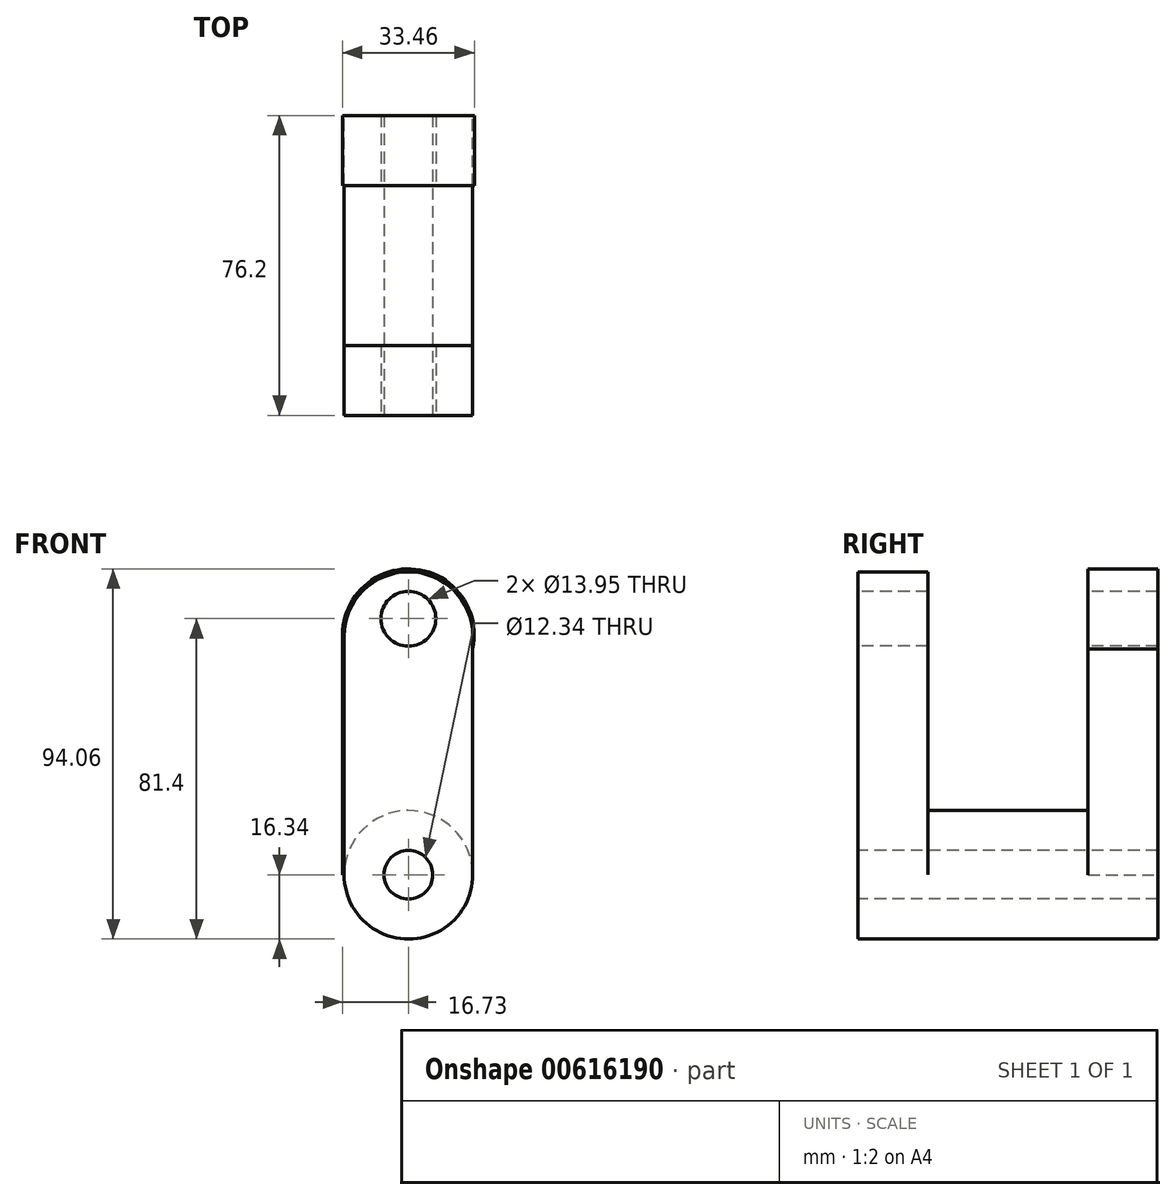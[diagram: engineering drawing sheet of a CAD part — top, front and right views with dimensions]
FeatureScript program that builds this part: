
annotation { "Feature Type Name" : "Feature", "Feature Type Description" : "" }
export const myFeature = defineFeature(function(context is Context, id is Id, definition is map)
    precondition{}
    {
        {
            var Q0;
            Q0=qCreatedBy(makeId("Front.planeOp"),FACE);
            var sketch = newSketch(context, id + "F0", { "sketchPlane" : qUnion([Q0])});
            skCircle(sketch, "E0", {"center": v(0, 0) * mm, "radius": 16.34 * mm});
            skSolve(sketch);
        }
        {
            var Q0;
            Q0 = qSketchRegion(id + "F0", true);
            extrude(context, id + "F1", {"entities" : qUnion([Q0]), "depth" : 38.1 * mm, "offsetDistance" : 25.4 * mm});
        }
        {
            var Q0;
            Q0 = qSketchRegion(id + "F0", true);
            extrude(context, id + "F2", {"entities" : qUnion([Q0]), "operationType" : NewBodyOperationType.ADD, "depth" : -38.1 * mm, "offsetDistance" : 25.4 * mm});
        }
        {
            var Q0;
            Q0=makeQuery(id+"F1.opExtrude","CAP_FACE",FACE,{"disambiguationData":[OSD([sQuery(id+"F0.wireOp",EDGE,"E0")])],"isStart":false});
            var sketch = newSketch(context, id + "F3", { "sketchPlane" : qUnion([Q0])});
            skLineSegment(sketch, "E1.bottom", {"start": v(-16.34, 0) * mm, "end": v(16.34, 0) * mm});
            skLineSegment(sketch, "E1.top", {"start": v(-16.34, 60.62) * mm, "end": v(16.34, 60.62) * mm});
            skLineSegment(sketch, "E1.left", {"start": v(-16.34, 0) * mm, "end": v(-16.34, 60.62) * mm});
            skLineSegment(sketch, "E1.right", {"start": v(16.34, 0) * mm, "end": v(16.34, 60.62) * mm});
            skCircle(sketch, "E2", {"center": v(0, 60.62) * mm, "radius": 16.34 * mm});
            skSolve(sketch);
        }
        {
            var Q0;
            Q0=makeQuery(id+"F2.opExtrude","CAP_FACE",FACE,{"disambiguationData":[OSD([sQuery(id+"F0.wireOp",EDGE,"E0")])],"isStart":false});
            var sketch = newSketch(context, id + "F4", { "sketchPlane" : qUnion([Q0])});
            skLineSegment(sketch, "E3.bottom", {"start": v(-16.34, 0) * mm, "end": v(16.73, 0) * mm});
            skLineSegment(sketch, "E3.top", {"start": v(-16.34, 61) * mm, "end": v(16.73, 61) * mm});
            skLineSegment(sketch, "E3.left", {"start": v(-16.34, 0) * mm, "end": v(-16.34, 61) * mm});
            skLineSegment(sketch, "E3.right", {"start": v(16.73, 0) * mm, "end": v(16.73, 61) * mm});
            skCircle(sketch, "E4", {"center": v(0, 61) * mm, "radius": 16.73 * mm});
            skSolve(sketch);
        }
        {
            var Q0;
            Q0 = qSketchRegion(id + "F3", true);
            extrude(context, id + "F5", {"entities" : qUnion([Q0]), "operationType" : NewBodyOperationType.ADD, "depth" : -17.78 * mm, "offsetDistance" : 25.4 * mm});
        }
        {
            var Q0;
            Q0 = qSketchRegion(id + "F4", true);
            extrude(context, id + "F6", {"entities" : qUnion([Q0]), "operationType" : NewBodyOperationType.ADD, "depth" : -17.78 * mm, "offsetDistance" : 25.4 * mm});
        }
        {
            var Q0;
            Q0=makeQuery(id+"F5.boolean.opBoolean","MERGE",FACE,{"derivedFrom":[makeQuery(id+"F1.opExtrude","CAP_FACE",FACE,{"disambiguationData":[OSD([sQuery(id+"F0.wireOp",EDGE,"E0")])],"isStart":false}),makeQuery(id+"F5.opExtrude","CAP_FACE",FACE,{"disambiguationData":[OSD([sQuery(id+"F3.wireOp",EDGE,"E1.bottom"),sQuery(id+"F3.wireOp",EDGE,"E1.left"),sQuery(id+"F3.wireOp",EDGE,"E1.right"),sQuery(id+"F3.wireOp",EDGE,"E2")])],"isStart":true})]});
            var sketch = newSketch(context, id + "F7", { "sketchPlane" : qUnion([Q0])});
            skCircle(sketch, "E5", {"center": v(0, 0) * mm, "radius": 6.17 * mm});
            skCircle(sketch, "E6", {"center": v(0, 65.06) * mm, "radius": 6.97 * mm});
            skSolve(sketch);
        }
        {
            var Q0;
            Q0 = qSketchRegion(id + "F7", true);
            extrude(context, id + "F8", {"entities" : qUnion([Q0]), "operationType" : NewBodyOperationType.REMOVE, "oppositeDirection" : true, "depth" : 152.4 * mm, "offsetDistance" : 25.4 * mm});
        }
    });
